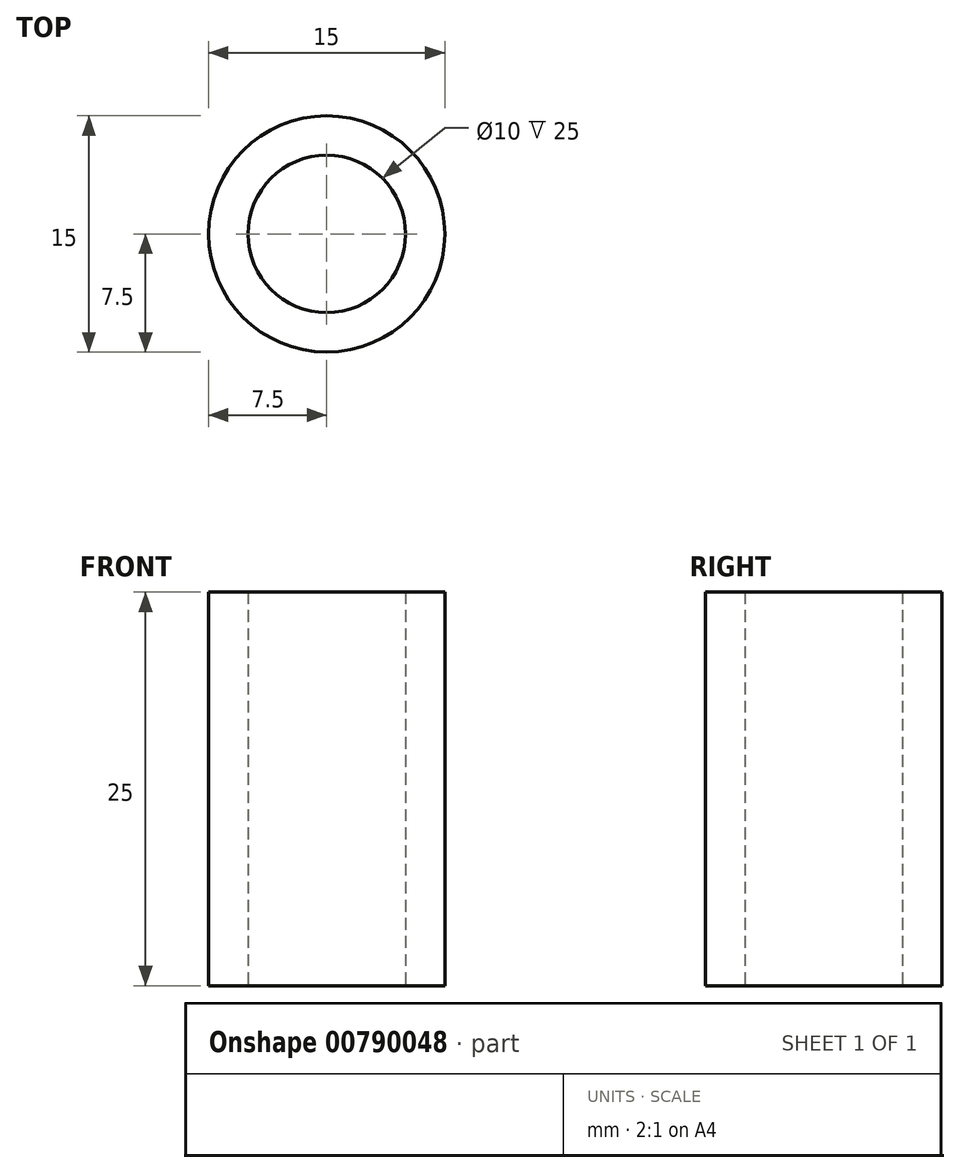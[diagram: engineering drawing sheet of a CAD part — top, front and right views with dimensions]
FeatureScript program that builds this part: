
annotation { "Feature Type Name" : "Feature", "Feature Type Description" : "" }
export const myFeature = defineFeature(function(context is Context, id is Id, definition is map)
    precondition{}
    {
        {
            var Q0;
            Q0=qCreatedBy(makeId("Top.planeOp"),FACE);
            var sketch = newSketch(context, id + "F0", { "sketchPlane" : qUnion([Q0])});
            skCircle(sketch, "E0", {"center": v(0, 0) * mm, "radius": 7.5 * mm});
            skCircle(sketch, "E1", {"center": v(0, 0) * mm, "radius": 5 * mm});
            skLineSegment(sketch, "E2", {"start": v(0, 7.5) * mm, "end": v(0, -7.5) * mm, "construction": true});
            skSolve(sketch);
        }
        {
            var Q0;
            Q0=qSketchRegion(id+"F0",true);
            extrude(context, id + "F1", {"entities" : qUnion([Q0]), "depth" : 25 * mm});
        }
        {
            var Q0;
            Q0=qCreatedBy(makeId("Front.planeOp"),FACE);
            cPlane(context, id + "F2", {"entities" : qUnion([Q0]), "cplaneType" : CPlaneType.OFFSET, "offset" : (15 / 2) * mm, "width" : 150 * mm, "height" : 150 * mm});
        }
    });
